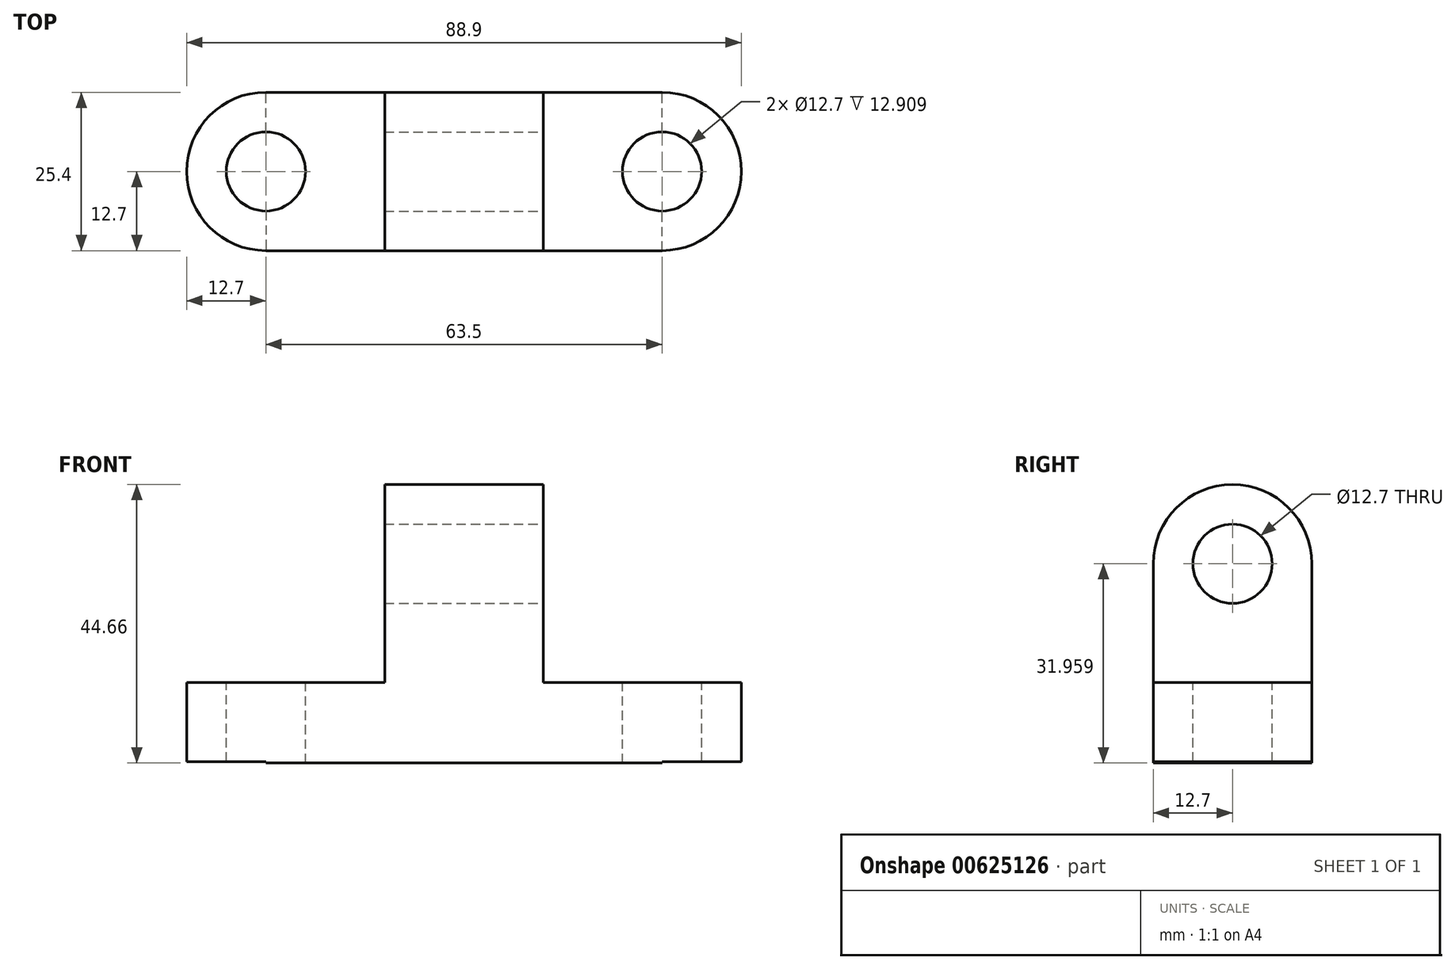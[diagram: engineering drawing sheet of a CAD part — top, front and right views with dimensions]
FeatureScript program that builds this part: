
annotation { "Feature Type Name" : "Feature", "Feature Type Description" : "" }
export const myFeature = defineFeature(function(context is Context, id is Id, definition is map)
    precondition{}
    {
        {
            var Q0;
            Q0=qCreatedBy(makeId("Front.planeOp"),FACE);
            var sketch = newSketch(context, id + "F0", { "sketchPlane" : qUnion([Q0])});
            skLineSegment(sketch, "E0", {"start": v(0, 0) * mm, "end": v(63.5, 0) * mm});
            skLineSegment(sketch, "E1", {"start": v(63.5, 0) * mm, "end": v(63.5, 38.1) * mm});
            skLineSegment(sketch, "E2", {"start": v(63.5, 38.1) * mm, "end": v(0, 38.1) * mm});
            skLineSegment(sketch, "E3", {"start": v(0, 38.1) * mm, "end": v(0, 0) * mm});
            skSolve(sketch);
        }
        {
            var Q0;
            Q0 = qSketchRegion(id + "F0", true);
            extrude(context, id + "F1", {"entities" : qUnion([Q0]), "depth" : 25.4 * mm, "offsetDistance" : 25.4 * mm});
        }
        {
            var Q0;
            Q0=makeQuery(id+"F1.opExtrude","CAP_FACE",FACE,{"disambiguationData":[OSD([sQuery(id+"F0.wireOp",EDGE,"E0"),sQuery(id+"F0.wireOp",EDGE,"E1"),sQuery(id+"F0.wireOp",EDGE,"E2"),sQuery(id+"F0.wireOp",EDGE,"E3")])],"isStart":false});
            var sketch = newSketch(context, id + "F2", { "sketchPlane" : qUnion([Q0])});
            skLineSegment(sketch, "E4", {"start": v(0, 0) * mm, "end": v(0, 12.9) * mm});
            skLineSegment(sketch, "E5", {"start": v(0, 12.9) * mm, "end": v(19.05, 12.9) * mm});
            skLineSegment(sketch, "E6", {"start": v(19.05, 12.9) * mm, "end": v(19.05, 31.96) * mm});
            skLineSegment(sketch, "E7", {"start": v(63.5, 0) * mm, "end": v(63.5, 12.9) * mm});
            skLineSegment(sketch, "E8", {"start": v(63.5, 12.9) * mm, "end": v(44.45, 12.9) * mm});
            skLineSegment(sketch, "E9", {"start": v(44.45, 12.9) * mm, "end": v(44.45, 31.96) * mm});
            skLineSegment(sketch, "E10", {"start": v(63.5, 0) * mm, "end": v(0, 0) * mm});
            skLineSegment(sketch, "E11", {"start": v(44.45, 31.96) * mm, "end": v(19.05, 31.96) * mm});
            skSolve(sketch);
        }
        {
            var Q0;
            {var subQ1=sQuery(id+"F2.wireOp",EDGE,"E5");Q0=makeQuery(id+"F2.imprint","IMPRINT",FACE,{"disambiguationData":[TD([[makeQuery(id+"F2.imprint","IMPRINT",EDGE,{"derivedFrom":subQ1}),1.0]])]});}
            extrude(context, id + "F3", {"entities" : qUnion([Q0]), "operationType" : NewBodyOperationType.REMOVE, "oppositeDirection" : true, "depth" : 25.4 * mm, "offsetDistance" : 25.4 * mm});
        }
        {
            var Q0;
            Q0=makeQuery(id+"F3.boolean.opBoolean","COPY",FACE,{"derivedFrom":makeQuery(id+"F3.opExtrude","SWEPT_FACE",FACE,{"disambiguationData":[OSD([sQuery(id+"F2.wireOp",EDGE,"E9")])]})});
            var sketch = newSketch(context, id + "F4", { "sketchPlane" : qUnion([Q0])});
            skArc(sketch, "E12", {"start": v(0, 31.96) * mm, "mid": v(-12.7, 44.66) * mm, "end": v(-25.4, 31.96) * mm});
            skSolve(sketch);
        }
        {
            var Q0;
            Q0=makeQuery(id+"F4.imprint","IMPRINT",FACE,{"disambiguationData":[TD([[makeQuery(id+"F4.imprint","IMPRINT",EDGE,{"derivedFrom":sQuery(id+"F4.wireOp",EDGE,"E12")}),1.0]])]});
            extrude(context, id + "F5", {"entities" : qUnion([Q0]), "operationType" : NewBodyOperationType.ADD, "oppositeDirection" : true, "depth" : 25.4 * mm, "offsetDistance" : 25.4 * mm});
        }
        {
            var Q0;
            Q0=makeQuery(id+"F3.boolean.opBoolean","COPY",FACE,{"derivedFrom":makeQuery(id+"F3.opExtrude","SWEPT_FACE",FACE,{"disambiguationData":[OSD([sQuery(id+"F2.wireOp",EDGE,"E5")])]})});
            var sketch = newSketch(context, id + "F6", { "sketchPlane" : qUnion([Q0])});
            skArc(sketch, "E13", {"start": v(0, 0) * mm, "mid": v(-12.7, -12.7) * mm, "end": v(0, -25.4) * mm});
            skLineSegment(sketch, "E14", {"start": v(0, -25.4) * mm, "end": v(0, 0) * mm});
            skSolve(sketch);
        }
        {
            var Q0;
            Q0=makeQuery(id+"F6.imprint","IMPRINT",FACE,{"disambiguationData":[TD([[makeQuery(id+"F6.imprint","IMPRINT",EDGE,{"derivedFrom":sQuery(id+"F6.wireOp",EDGE,"E13")}),1.0]])]});
            extrude(context, id + "F7", {"entities" : qUnion([Q0]), "operationType" : NewBodyOperationType.ADD, "oppositeDirection" : true, "depth" : 12.7 * mm, "offsetDistance" : 25.4 * mm});
        }
        {
            var Q0;
            Q0=makeQuery(id+"F3.boolean.opBoolean","COPY",FACE,{"derivedFrom":makeQuery(id+"F3.opExtrude","SWEPT_FACE",FACE,{"disambiguationData":[OSD([sQuery(id+"F2.wireOp",EDGE,"E8")])]})});
            var sketch = newSketch(context, id + "F8", { "sketchPlane" : qUnion([Q0])});
            skArc(sketch, "E15", {"start": v(63.5, -25.4) * mm, "mid": v(76.2, -12.7) * mm, "end": v(63.5, 0) * mm});
            skLineSegment(sketch, "E16", {"start": v(63.5, 0) * mm, "end": v(63.5, -25.4) * mm});
            skSolve(sketch);
        }
        {
            var Q0;
            Q0=makeQuery(id+"F8.imprint","IMPRINT",FACE,{"disambiguationData":[TD([[makeQuery(id+"F8.imprint","IMPRINT",EDGE,{"derivedFrom":sQuery(id+"F8.wireOp",EDGE,"E15")}),1.0]])]});
            extrude(context, id + "F9", {"entities" : qUnion([Q0]), "operationType" : NewBodyOperationType.ADD, "oppositeDirection" : true, "depth" : 12.7 * mm, "offsetDistance" : 25.4 * mm});
        }
        {
            var Q0;
            {var subQ0=sQuery(id+"F2.wireOp",EDGE,"E9");Q0=makeQuery(id+"F5.boolean.opBoolean","MERGE",FACE,{"derivedFrom":[makeQuery(id+"F3.boolean.opBoolean","COPY",FACE,{"derivedFrom":makeQuery(id+"F3.opExtrude","SWEPT_FACE",FACE,{"disambiguationData":[OSD([subQ0])]})}),makeQuery(id+"F5.opExtrude","CAP_FACE",FACE,{"disambiguationData":[OSD([subQ0,sQuery(id+"F2.wireOp",EDGE,"E11"),sQuery(id+"F4.wireOp",EDGE,"E12")])],"isStart":true})]});}
            var sketch = newSketch(context, id + "F10", { "sketchPlane" : qUnion([Q0])});
            skCircle(sketch, "E17", {"center": v(-12.7, 31.96) * mm, "radius": 6.35 * mm});
            skSolve(sketch);
        }
        {
            var Q0;
            Q0=makeQuery(id+"F10.imprint","IMPRINT",FACE,{"disambiguationData":[TD([[makeQuery(id+"F10.imprint","IMPRINT",EDGE,{"derivedFrom":sQuery(id+"F10.wireOp",EDGE,"E17")}),1.0]])]});
            extrude(context, id + "F11", {"entities" : qUnion([Q0]), "operationType" : NewBodyOperationType.REMOVE, "oppositeDirection" : true, "depth" : 25.4 * mm, "offsetDistance" : 25.4 * mm});
        }
        {
            var Q0;
            Q0=makeQuery(id+"F9.boolean.opBoolean","MERGE",FACE,{"derivedFrom":[makeQuery(id+"F3.boolean.opBoolean","COPY",FACE,{"derivedFrom":makeQuery(id+"F3.opExtrude","SWEPT_FACE",FACE,{"disambiguationData":[OSD([sQuery(id+"F2.wireOp",EDGE,"E8")])]})}),makeQuery(id+"F9.opExtrude","CAP_FACE",FACE,{"disambiguationData":[OSD([sQuery(id+"F8.wireOp",EDGE,"E15"),sQuery(id+"F8.wireOp",EDGE,"E16")])],"isStart":true})]});
            var sketch = newSketch(context, id + "F12", { "sketchPlane" : qUnion([Q0])});
            skCircle(sketch, "E18", {"center": v(63.5, -12.7) * mm, "radius": 6.35 * mm});
            skSolve(sketch);
        }
        {
            var Q0;
            Q0=makeQuery(id+"F12.imprint","IMPRINT",FACE,{"disambiguationData":[TD([[makeQuery(id+"F12.imprint","IMPRINT",EDGE,{"derivedFrom":sQuery(id+"F12.wireOp",EDGE,"E18")}),1.0]])]});
            extrude(context, id + "F13", {"entities" : qUnion([Q0]), "operationType" : NewBodyOperationType.REMOVE, "oppositeDirection" : true, "depth" : 25.4 * mm, "offsetDistance" : 25.4 * mm});
        }
        {
            var Q0;
            Q0=makeQuery(id+"F7.boolean.opBoolean","MERGE",FACE,{"derivedFrom":[makeQuery(id+"F3.boolean.opBoolean","COPY",FACE,{"derivedFrom":makeQuery(id+"F3.opExtrude","SWEPT_FACE",FACE,{"disambiguationData":[OSD([sQuery(id+"F2.wireOp",EDGE,"E5")])]})}),makeQuery(id+"F7.opExtrude","CAP_FACE",FACE,{"disambiguationData":[OSD([sQuery(id+"F6.wireOp",EDGE,"E13"),sQuery(id+"F6.wireOp",EDGE,"E14")])],"isStart":true})]});
            var sketch = newSketch(context, id + "F14", { "sketchPlane" : qUnion([Q0])});
            skCircle(sketch, "E19", {"center": v(0, -12.7) * mm, "radius": 6.35 * mm});
            skSolve(sketch);
        }
        {
            var Q0;
            Q0=makeQuery(id+"F14.imprint","IMPRINT",FACE,{"disambiguationData":[TD([[makeQuery(id+"F14.imprint","IMPRINT",EDGE,{"derivedFrom":sQuery(id+"F14.wireOp",EDGE,"E19")}),1.0]])]});
            extrude(context, id + "F15", {"entities" : qUnion([Q0]), "operationType" : NewBodyOperationType.REMOVE, "oppositeDirection" : true, "depth" : 25.4 * mm, "offsetDistance" : 25.4 * mm});
        }
    });
